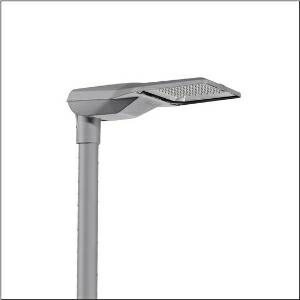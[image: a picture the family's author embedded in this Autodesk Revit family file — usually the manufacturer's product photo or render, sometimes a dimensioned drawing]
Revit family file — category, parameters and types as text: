
# Revit family: streetlight_sl_21_iq_midi___st1_0a_5xe3d41d08nb_8ddf
name_source: partatom
category: Lighting Fixtures
units: mm (PartAtom-declared; Revit-internal decimal feet)

## family parameters
Cut with Voids When Loaded = No
Host = Face
Light Source = No
Part Type = Normal
Room Calculation Point = No
Round Connector Dimension = Use Diameter
Shared = No

## types (1)
- --- (1 x LED, 24250 lm, 155.5 W, 4000K)
    Apparent Load = 155 VA
    CIE Flux Codes = 40 73 97 100 100
    Color Rendering = 70
    Color Temperature = 4000K
    Default Elevation = 1800 mm
    Description = Streetlight SL 21 iQ midi, mast luminaire, primary light control with lens, of PMMA, primary optical cover: cover, of toughened safety glass, transparent, light distribution: ST1.0a, light emission: direct distribution, primary light characteristic: asymmetric, installation type: post-top, side-entry, LED, High Power LED, rated luminous flux: 24.250lm, luminous efficacy: 156lm/W, light colour: 740, colour temperature: 4000K, control gear: iQ-Comfort, control: Auto-Match, Temp-Guard, Lumen-Switch, Night-Set, Smart-Wire, Light-Fading, Desk-Remote (wireless, voltage-free reading and setting of iQ features in the workshop via application-optimized NFC function/RFID function), optimised constant luminous flux control (CLO 2.0), pre-setting: linear dimming characteristic, mains connection: 230..240V, AC, 50/60Hz, start of lifetime: 156W, end of service life: 162W, reduction: 69W, luminaire housing, of diecast aluminium, powder-coated, SITECO metallic grey (DB 702S), corrosivity category C5 high according to DIN EN ISO 12944, please order mast flange separately, inclination adjustable: 0°, 5°, 10°, 15°, sealing non-destructively replaceable, multi-level sealing system, length: 644mm, width: 335mm, height: 110mm, mast flange for spigot size: 42mm (side-entry): 5XC10008XM4, 60/48mm (side-entry/post-top): 5XC10108XM2, 76/60mm (side-entry/post-top): 5XC10108XM1, mounting height: 4..8m, protection rating (complete): IP66, insulation class (complete): insulation class II (safety insulation), certification: CE, ENEC, ENEC+, VDE, impact resistance: IK10, permissible operating ambient temperature for outdoor applications: -40..+50°C, standard-compliant lighting for roads and squares, packaging unit: 1 piece

Light Distribution: ST1.0a
    Height = 111 mm
    Lamp = 1 x LED
    Lamp Light Flux = 24250 lm
    Lamp Power = 155.5 W
    Lamp count = 1
    Length = 644 mm
    Luminous efficacy = 156 lm/W
    Manufacturer = Siteco
    ModVariant = No
    Model = 5XE3D41D08NB
    Number of Poles = 1
    OnlyDefault = Yes
    Power Factor = 1
    Product Name = Streetlight SL 21 iQ midi | ST1.0a
    Product group = mast luminaire | pylon top
    ProductGroupID = 6100
    Protection Class = Protection class II
    Protection Degree = IP 66
    RLX_Detail_Level = 1
    RLX_Emergency_Light_Flux = 0 lm
    RLX_Emergency_Type = 0
    RLX_Emergency_Type_DB = No
    RlxData = <blob elided: 27185 chars, md5=e81a9469>
    Socket = socket
    Standby Power = 0 W
    System Light Flux = 24250 lm
    System Power = 155 W
    Type Comments = factory setting: luminous flux: 100 % | dim-lin: 254 | 823 mA
    Type Image = l_1004298.jpg
    URL = http://relux.com
    VarID = @adj_170287
    Voltage = 0 V
    Weight = 0.00 kg
    Width = 336 mm

## geometry (parser evidence)
native form markers: Blend x4, Sweep x9
no freeform markers — native parametric forms only
